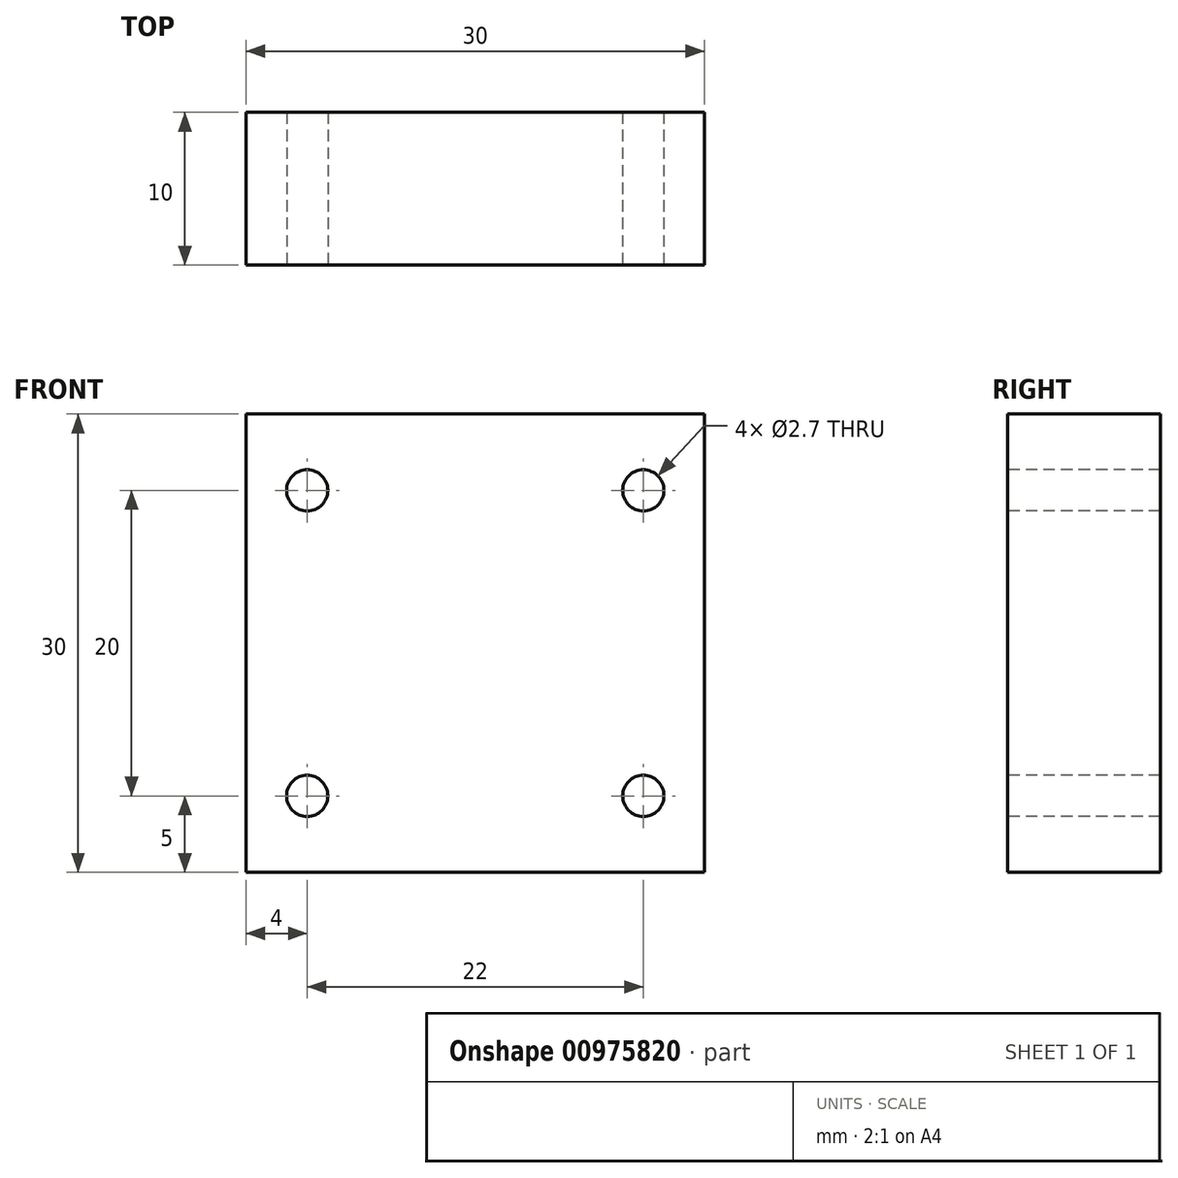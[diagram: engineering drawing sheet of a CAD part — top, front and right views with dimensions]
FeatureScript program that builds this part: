
annotation { "Feature Type Name" : "Feature", "Feature Type Description" : "" }
export const myFeature = defineFeature(function(context is Context, id is Id, definition is map)
    precondition{}
    {
        {
            var Q0;
            Q0=qCreatedBy(makeId("Front.planeOp"),FACE);
            var sketch = newSketch(context, id + "F0", { "sketchPlane" : qUnion([Q0])});
            skLineSegment(sketch, "E0.bottom", {"start": v(0, 0) * mm, "end": v(30, 0) * mm});
            skLineSegment(sketch, "E0.top", {"start": v(0, -30) * mm, "end": v(30, -30) * mm});
            skLineSegment(sketch, "E0.left", {"start": v(0, 0) * mm, "end": v(0, -30) * mm});
            skLineSegment(sketch, "E0.right", {"start": v(30, 0) * mm, "end": v(30, -30) * mm});
            skSolve(sketch);
        }
        {
            var Q0;
            Q0 = qSketchRegion(id + "F0", true);
            extrude(context, id + "F1", {"entities" : qUnion([Q0]), "depth" : 10 * mm, "offsetDistance" : 25 * mm});
        }
        {
            var Q0;
            Q0=makeQuery(id+"F1.opExtrude","CAP_FACE",FACE,{"disambiguationData":[OSD([sQuery(id+"F0.wireOp",EDGE,"E0.bottom"),sQuery(id+"F0.wireOp",EDGE,"E0.top"),sQuery(id+"F0.wireOp",EDGE,"E0.left"),sQuery(id+"F0.wireOp",EDGE,"E0.right")])],"isStart":false});
            var sketch = newSketch(context, id + "F2", { "sketchPlane" : qUnion([Q0])});
            skLineSegment(sketch, "E1.bottom", {"start": v(0, 0) * mm, "end": v(30, 0) * mm});
            skLineSegment(sketch, "E1.top", {"start": v(0, -10) * mm, "end": v(30, -10) * mm});
            skLineSegment(sketch, "E1.left", {"start": v(0, 0) * mm, "end": v(0, -10) * mm});
            skLineSegment(sketch, "E1.right", {"start": v(30, 0) * mm, "end": v(30, -10) * mm});
            skLineSegment(sketch, "E2.bottom", {"start": v(0, -30) * mm, "end": v(30, -30) * mm});
            skLineSegment(sketch, "E2.top", {"start": v(0, -20) * mm, "end": v(30, -20) * mm});
            skLineSegment(sketch, "E2.left", {"start": v(0, -30) * mm, "end": v(0, -20) * mm});
            skLineSegment(sketch, "E2.right", {"start": v(30, -30) * mm, "end": v(30, -20) * mm});
            skLineSegment(sketch, "E3.bottom", {"start": v(0, 0) * mm, "end": v(8, 0) * mm});
            skLineSegment(sketch, "E3.top", {"start": v(0, -10) * mm, "end": v(8, -10) * mm});
            skLineSegment(sketch, "E3.right", {"start": v(8, 0) * mm, "end": v(8, -10) * mm});
            skLineSegment(sketch, "E4.bottom", {"start": v(30, 0) * mm, "end": v(22, 0) * mm});
            skLineSegment(sketch, "E4.top", {"start": v(30, -10) * mm, "end": v(22, -10) * mm});
            skLineSegment(sketch, "E4.right", {"start": v(22, 0) * mm, "end": v(22, -10) * mm});
            skLineSegment(sketch, "E5.bottom", {"start": v(0, -30) * mm, "end": v(8, -30) * mm});
            skLineSegment(sketch, "E5.top", {"start": v(0, -20) * mm, "end": v(8, -20) * mm});
            skLineSegment(sketch, "E5.right", {"start": v(8, -30) * mm, "end": v(8, -20) * mm});
            skLineSegment(sketch, "E6.bottom", {"start": v(22, -20) * mm, "end": v(30, -20) * mm});
            skLineSegment(sketch, "E6.top", {"start": v(22, -30) * mm, "end": v(30, -30) * mm});
            skLineSegment(sketch, "E6.left", {"start": v(22, -20) * mm, "end": v(22, -30) * mm});
            skLineSegment(sketch, "E6.right", {"start": v(30, -20) * mm, "end": v(30, -30) * mm});
            skLineSegment(sketch, "E7", {"start": v(0, -5) * mm, "end": v(8, -5) * mm});
            skLineSegment(sketch, "E8", {"start": v(8, -5) * mm, "end": v(22, -5) * mm});
            skLineSegment(sketch, "E9", {"start": v(22, -5) * mm, "end": v(30, -5) * mm});
            skLineSegment(sketch, "E10", {"start": v(0, -25) * mm, "end": v(8, -25) * mm});
            skLineSegment(sketch, "E11", {"start": v(8, -25) * mm, "end": v(22, -25) * mm});
            skLineSegment(sketch, "E12", {"start": v(22, -25) * mm, "end": v(30, -25) * mm});
            skCircle(sketch, "E13", {"center": v(4, -5) * mm, "radius": 4 * mm});
            skCircle(sketch, "E14", {"center": v(26, -5) * mm, "radius": 4 * mm});
            skCircle(sketch, "E15", {"center": v(4, -25) * mm, "radius": 4 * mm});
            skCircle(sketch, "E16", {"center": v(26, -25) * mm, "radius": 4 * mm});
            skCircle(sketch, "E17", {"center": v(4, -5) * mm, "radius": 1.35 * mm});
            skCircle(sketch, "E18", {"center": v(26, -5) * mm, "radius": 1.35 * mm});
            skCircle(sketch, "E19", {"center": v(4, -25) * mm, "radius": 1.35 * mm});
            skCircle(sketch, "E20", {"center": v(26, -25) * mm, "radius": 1.35 * mm});
            skSolve(sketch);
        }
        {
            var Q0;
            {var subQ0=sQuery(id+"F2.wireOp",EDGE,"E19");var subQ1=sQuery(id+"F2.wireOp",EDGE,"E10");var subQ2=makeQuery(id+"F2.imprint","INTERSECT",VERTEX,{"disambiguationData":[OD(0.0)],"derivedFrom":[subQ1,subQ0]});Q0=makeQuery(id+"F2.imprint","IMPRINT",FACE,{"disambiguationData":[TD([[makeQuery(id+"F2.imprint","IMPRINT",EDGE,{"disambiguationData":[TD([[subQ2,-1.0]])],"derivedFrom":subQ1}),1.0]])]});}
            var Q1;
            {var subQ0=sQuery(id+"F2.wireOp",EDGE,"E19");var subQ1=sQuery(id+"F2.wireOp",EDGE,"E10");var subQ2=makeQuery(id+"F2.imprint","INTERSECT",VERTEX,{"disambiguationData":[OD(0.0)],"derivedFrom":[subQ1,subQ0]});Q1=makeQuery(id+"F2.imprint","IMPRINT",FACE,{"disambiguationData":[TD([[makeQuery(id+"F2.imprint","IMPRINT",EDGE,{"disambiguationData":[TD([[subQ2,-1.0]])],"derivedFrom":subQ1}),-1.0]])]});}
            var Q2;
            {var subQ0=sQuery(id+"F2.wireOp",EDGE,"E20");var subQ1=sQuery(id+"F2.wireOp",EDGE,"E12");var subQ2=makeQuery(id+"F2.imprint","INTERSECT",VERTEX,{"disambiguationData":[OD(0.0)],"derivedFrom":[subQ1,subQ0]});Q2=makeQuery(id+"F2.imprint","IMPRINT",FACE,{"disambiguationData":[TD([[makeQuery(id+"F2.imprint","IMPRINT",EDGE,{"disambiguationData":[TD([[subQ2,-1.0]])],"derivedFrom":subQ1}),1.0]])]});}
            var Q3;
            {var subQ0=sQuery(id+"F2.wireOp",EDGE,"E20");var subQ1=sQuery(id+"F2.wireOp",EDGE,"E12");var subQ2=makeQuery(id+"F2.imprint","INTERSECT",VERTEX,{"disambiguationData":[OD(0.0)],"derivedFrom":[subQ1,subQ0]});Q3=makeQuery(id+"F2.imprint","IMPRINT",FACE,{"disambiguationData":[TD([[makeQuery(id+"F2.imprint","IMPRINT",EDGE,{"disambiguationData":[TD([[subQ2,-1.0]])],"derivedFrom":subQ1}),-1.0]])]});}
            var Q4;
            {var subQ0=sQuery(id+"F2.wireOp",EDGE,"E18");var subQ1=sQuery(id+"F2.wireOp",EDGE,"E9");var subQ2=makeQuery(id+"F2.imprint","INTERSECT",VERTEX,{"disambiguationData":[OD(0.0)],"derivedFrom":[subQ1,subQ0]});Q4=makeQuery(id+"F2.imprint","IMPRINT",FACE,{"disambiguationData":[TD([[makeQuery(id+"F2.imprint","IMPRINT",EDGE,{"disambiguationData":[TD([[subQ2,-1.0]])],"derivedFrom":subQ1}),-1.0]])]});}
            var Q5;
            {var subQ0=sQuery(id+"F2.wireOp",EDGE,"E18");var subQ1=sQuery(id+"F2.wireOp",EDGE,"E9");var subQ2=makeQuery(id+"F2.imprint","INTERSECT",VERTEX,{"disambiguationData":[OD(0.0)],"derivedFrom":[subQ1,subQ0]});Q5=makeQuery(id+"F2.imprint","IMPRINT",FACE,{"disambiguationData":[TD([[makeQuery(id+"F2.imprint","IMPRINT",EDGE,{"disambiguationData":[TD([[subQ2,-1.0]])],"derivedFrom":subQ1}),1.0]])]});}
            var Q6;
            {var subQ0=sQuery(id+"F2.wireOp",EDGE,"E17");var subQ1=sQuery(id+"F2.wireOp",EDGE,"E7");var subQ2=makeQuery(id+"F2.imprint","INTERSECT",VERTEX,{"disambiguationData":[OD(0.0)],"derivedFrom":[subQ1,subQ0]});Q6=makeQuery(id+"F2.imprint","IMPRINT",FACE,{"disambiguationData":[TD([[makeQuery(id+"F2.imprint","IMPRINT",EDGE,{"disambiguationData":[TD([[subQ2,-1.0]])],"derivedFrom":subQ1}),-1.0]])]});}
            var Q7;
            {var subQ0=sQuery(id+"F2.wireOp",EDGE,"E17");var subQ1=sQuery(id+"F2.wireOp",EDGE,"E7");var subQ2=makeQuery(id+"F2.imprint","INTERSECT",VERTEX,{"disambiguationData":[OD(0.0)],"derivedFrom":[subQ1,subQ0]});Q7=makeQuery(id+"F2.imprint","IMPRINT",FACE,{"disambiguationData":[TD([[makeQuery(id+"F2.imprint","IMPRINT",EDGE,{"disambiguationData":[TD([[subQ2,-1.0]])],"derivedFrom":subQ1}),1.0]])]});}
            var Q8;
            Q8=sQuery(id+"F2.wireOp",EDGE,"E19");
            extrude(context, id + "F3", {"entities" : qUnion([Q0, Q1, Q2, Q3, Q4, Q5, Q6, Q7]), "operationType" : NewBodyOperationType.REMOVE, "surfaceEntities" : qUnion([Q8]), "oppositeDirection" : true, "depth" : 25 * mm, "offsetDistance" : 25 * mm});
        }
    });
